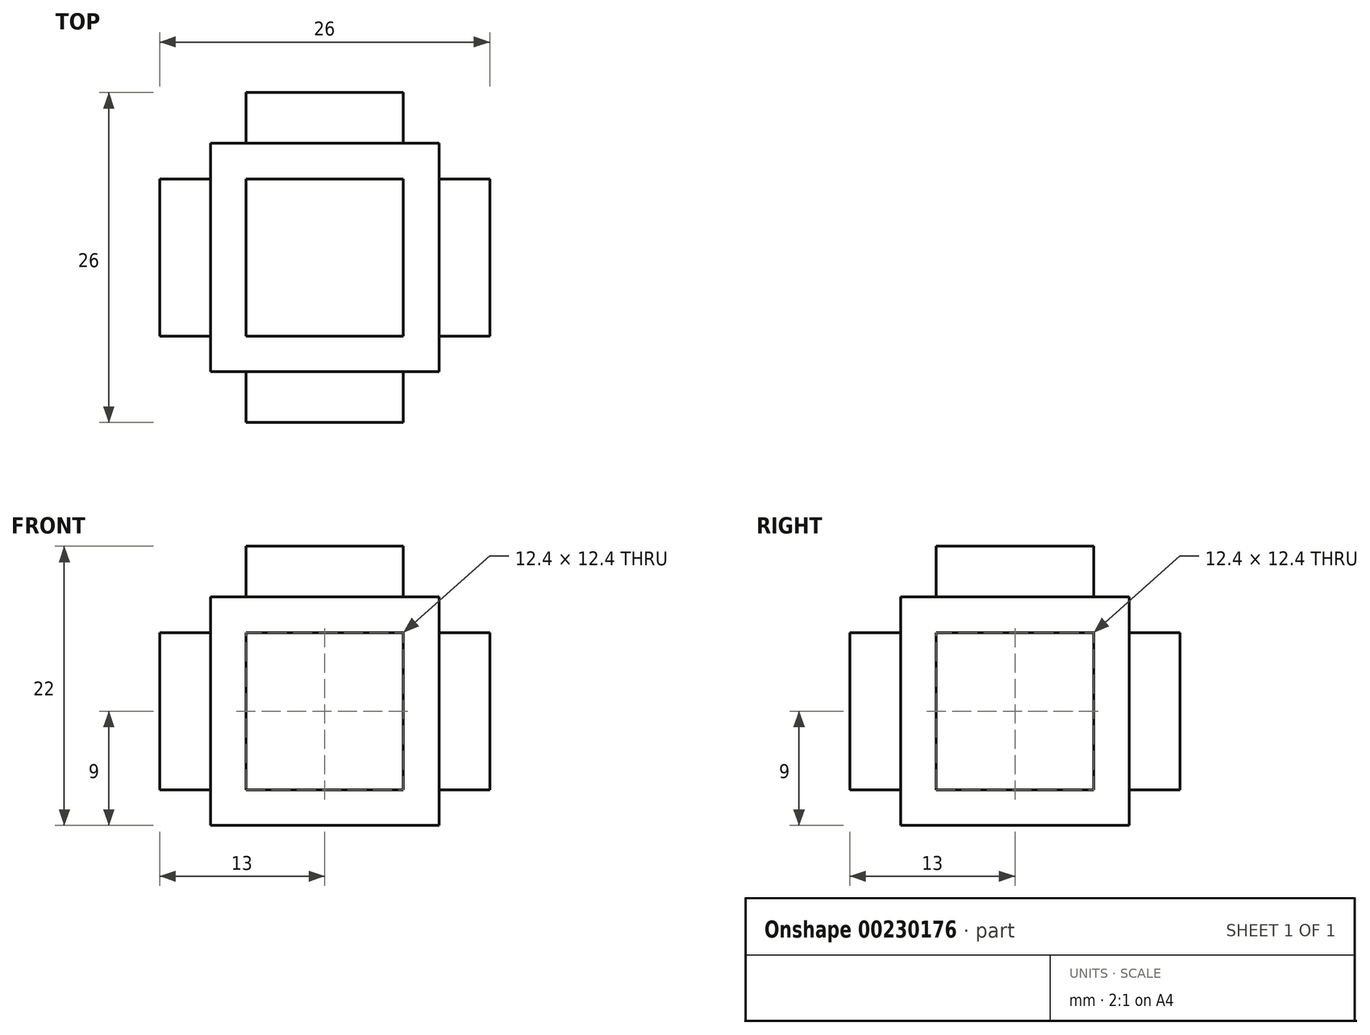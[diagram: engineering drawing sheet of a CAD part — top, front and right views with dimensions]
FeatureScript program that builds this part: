
annotation { "Feature Type Name" : "Feature", "Feature Type Description" : "" }
export const myFeature = defineFeature(function(context is Context, id is Id, definition is map)
    precondition{}
    {
        {
            var Q0;
            Q0=qCreatedBy(makeId("Top.planeOp"),FACE);
            var sketch = newSketch(context, id + "F0", { "sketchPlane" : qUnion([Q0])});
            skLineSegment(sketch, "E0.bottom", {"start": v(9, -9) * mm, "end": v(-9, -9) * mm});
            skLineSegment(sketch, "E0.top", {"start": v(9, 9) * mm, "end": v(-9, 9) * mm});
            skLineSegment(sketch, "E0.left", {"start": v(9, -9) * mm, "end": v(9, 9) * mm});
            skLineSegment(sketch, "E0.right", {"start": v(-9, -9) * mm, "end": v(-9, 9) * mm});
            skPoint(sketch, "E0.middle", {"position": v(0, 0) * mm});
            skSolve(sketch);
        }
        {
            var Q0;
            Q0 = qSketchRegion(id + "F0", true);
            extrude(context, id + "F1", {"entities" : qUnion([Q0]), "depth" : 18 * mm});
        }
        {
            var Q0;
            Q0=makeQuery(id+"F1.opExtrude","CAP_FACE",FACE,{"disambiguationData":[OSD([sQuery(id+"F0.wireOp",EDGE,"E0.bottom"),sQuery(id+"F0.wireOp",EDGE,"E0.top"),sQuery(id+"F0.wireOp",EDGE,"E0.left"),sQuery(id+"F0.wireOp",EDGE,"E0.right")])],"isStart":false});
            var sketch = newSketch(context, id + "F2", { "sketchPlane" : qUnion([Q0])});
            skLineSegment(sketch, "E1.bottom", {"start": v(6.2, 6.2) * mm, "end": v(-6.2, 6.2) * mm});
            skLineSegment(sketch, "E1.top", {"start": v(6.2, -6.2) * mm, "end": v(-6.2, -6.2) * mm});
            skLineSegment(sketch, "E1.left", {"start": v(6.2, 6.2) * mm, "end": v(6.2, -6.2) * mm});
            skLineSegment(sketch, "E1.right", {"start": v(-6.2, 6.2) * mm, "end": v(-6.2, -6.2) * mm});
            skPoint(sketch, "E1.middle", {"position": v(0, 0) * mm});
            skSolve(sketch);
        }
        {
            var Q0;
            Q0 = qSketchRegion(id + "F2", true);
            extrude(context, id + "F3", {"entities" : qUnion([Q0]), "operationType" : NewBodyOperationType.ADD, "depth" : 4 * mm});
        }
        {
            var Q0;
            Q0 = qSketchRegion(id + "F2", true);
            extrude(context, id + "F4", {"entities" : qUnion([Q0]), "operationType" : NewBodyOperationType.ADD, "oppositeDirection" : true, "depth" : 4 * mm});
        }
        {
            var Q0;
            Q0=makeQuery(id+"F1.opExtrude","SWEPT_FACE",FACE,{"disambiguationData":[OSD([sQuery(id+"F0.wireOp",EDGE,"E0.bottom")])]});
            var sketch = newSketch(context, id + "F5", { "sketchPlane" : qUnion([Q0])});
            skLineSegment(sketch, "E2", {"start": v(0, 18) * mm, "end": v(0, 0) * mm});
            skLineSegment(sketch, "E3.bottom", {"start": v(6.2, 2.8) * mm, "end": v(-6.2, 2.8) * mm});
            skLineSegment(sketch, "E3.top", {"start": v(6.2, 15.2) * mm, "end": v(-6.2, 15.2) * mm});
            skLineSegment(sketch, "E3.left", {"start": v(6.2, 2.8) * mm, "end": v(6.2, 15.2) * mm});
            skLineSegment(sketch, "E3.right", {"start": v(-6.2, 2.8) * mm, "end": v(-6.2, 15.2) * mm});
            skPoint(sketch, "E3.middle", {"position": v(0, 9) * mm});
            skSolve(sketch);
        }
        {
            var Q0;
            Q0 = qSketchRegion(id + "F5", true);
            extrude(context, id + "F6", {"entities" : qUnion([Q0]), "operationType" : NewBodyOperationType.ADD, "depth" : 4 * mm});
        }
        {
            var Q0;
            Q0=makeQuery(id+"F1.opExtrude","SWEPT_FACE",FACE,{"disambiguationData":[OSD([sQuery(id+"F0.wireOp",EDGE,"E0.right")])]});
            var sketch = newSketch(context, id + "F7", { "sketchPlane" : qUnion([Q0])});
            skLineSegment(sketch, "E4", {"start": v(0, 18) * mm, "end": v(0, 0) * mm});
            skLineSegment(sketch, "E5.bottom", {"start": v(6.2, 2.8) * mm, "end": v(-6.2, 2.8) * mm});
            skLineSegment(sketch, "E5.top", {"start": v(6.2, 15.2) * mm, "end": v(-6.2, 15.2) * mm});
            skLineSegment(sketch, "E5.left", {"start": v(6.2, 2.8) * mm, "end": v(6.2, 15.2) * mm});
            skLineSegment(sketch, "E5.right", {"start": v(-6.2, 2.8) * mm, "end": v(-6.2, 15.2) * mm});
            skPoint(sketch, "E5.middle", {"position": v(0, 9) * mm});
            skSolve(sketch);
        }
        {
            var Q0;
            Q0 = qSketchRegion(id + "F7", true);
            extrude(context, id + "F8", {"entities" : qUnion([Q0]), "operationType" : NewBodyOperationType.ADD, "depth" : 4 * mm});
        }
        {
            var Q0;
            Q0=makeQuery(id+"F1.opExtrude","SWEPT_FACE",FACE,{"disambiguationData":[OSD([sQuery(id+"F0.wireOp",EDGE,"E0.left")])]});
            var sketch = newSketch(context, id + "F9", { "sketchPlane" : qUnion([Q0])});
            skLineSegment(sketch, "E6", {"start": v(0, 18) * mm, "end": v(0, 0) * mm});
            skLineSegment(sketch, "E7.bottom", {"start": v(6.2, 15.2) * mm, "end": v(-6.2, 15.2) * mm});
            skLineSegment(sketch, "E7.top", {"start": v(6.2, 2.8) * mm, "end": v(-6.2, 2.8) * mm});
            skLineSegment(sketch, "E7.left", {"start": v(6.2, 15.2) * mm, "end": v(6.2, 2.8) * mm});
            skLineSegment(sketch, "E7.right", {"start": v(-6.2, 15.2) * mm, "end": v(-6.2, 2.8) * mm});
            skPoint(sketch, "E7.middle", {"position": v(0, 9) * mm});
            skSolve(sketch);
        }
        {
            var Q0;
            Q0 = qSketchRegion(id + "F9", true);
            extrude(context, id + "F10", {"entities" : qUnion([Q0]), "operationType" : NewBodyOperationType.ADD, "depth" : 4 * mm});
        }
        {
            var Q0;
            Q0=makeQuery(id+"F1.opExtrude","SWEPT_FACE",FACE,{"disambiguationData":[OSD([sQuery(id+"F0.wireOp",EDGE,"E0.top")])]});
            var sketch = newSketch(context, id + "F11", { "sketchPlane" : qUnion([Q0])});
            skLineSegment(sketch, "E8", {"start": v(0, 18) * mm, "end": v(0, 0) * mm});
            skLineSegment(sketch, "E9.bottom", {"start": v(6.2, 15.2) * mm, "end": v(-6.2, 15.2) * mm});
            skLineSegment(sketch, "E9.top", {"start": v(6.2, 2.8) * mm, "end": v(-6.2, 2.8) * mm});
            skLineSegment(sketch, "E9.left", {"start": v(6.2, 15.2) * mm, "end": v(6.2, 2.8) * mm});
            skLineSegment(sketch, "E9.right", {"start": v(-6.2, 15.2) * mm, "end": v(-6.2, 2.8) * mm});
            skPoint(sketch, "E9.middle", {"position": v(0, 9) * mm});
            skSolve(sketch);
        }
        {
            var Q0;
            Q0 = qSketchRegion(id + "F11", true);
            extrude(context, id + "F12", {"entities" : qUnion([Q0]), "operationType" : NewBodyOperationType.ADD, "depth" : 4 * mm});
        }
    });
